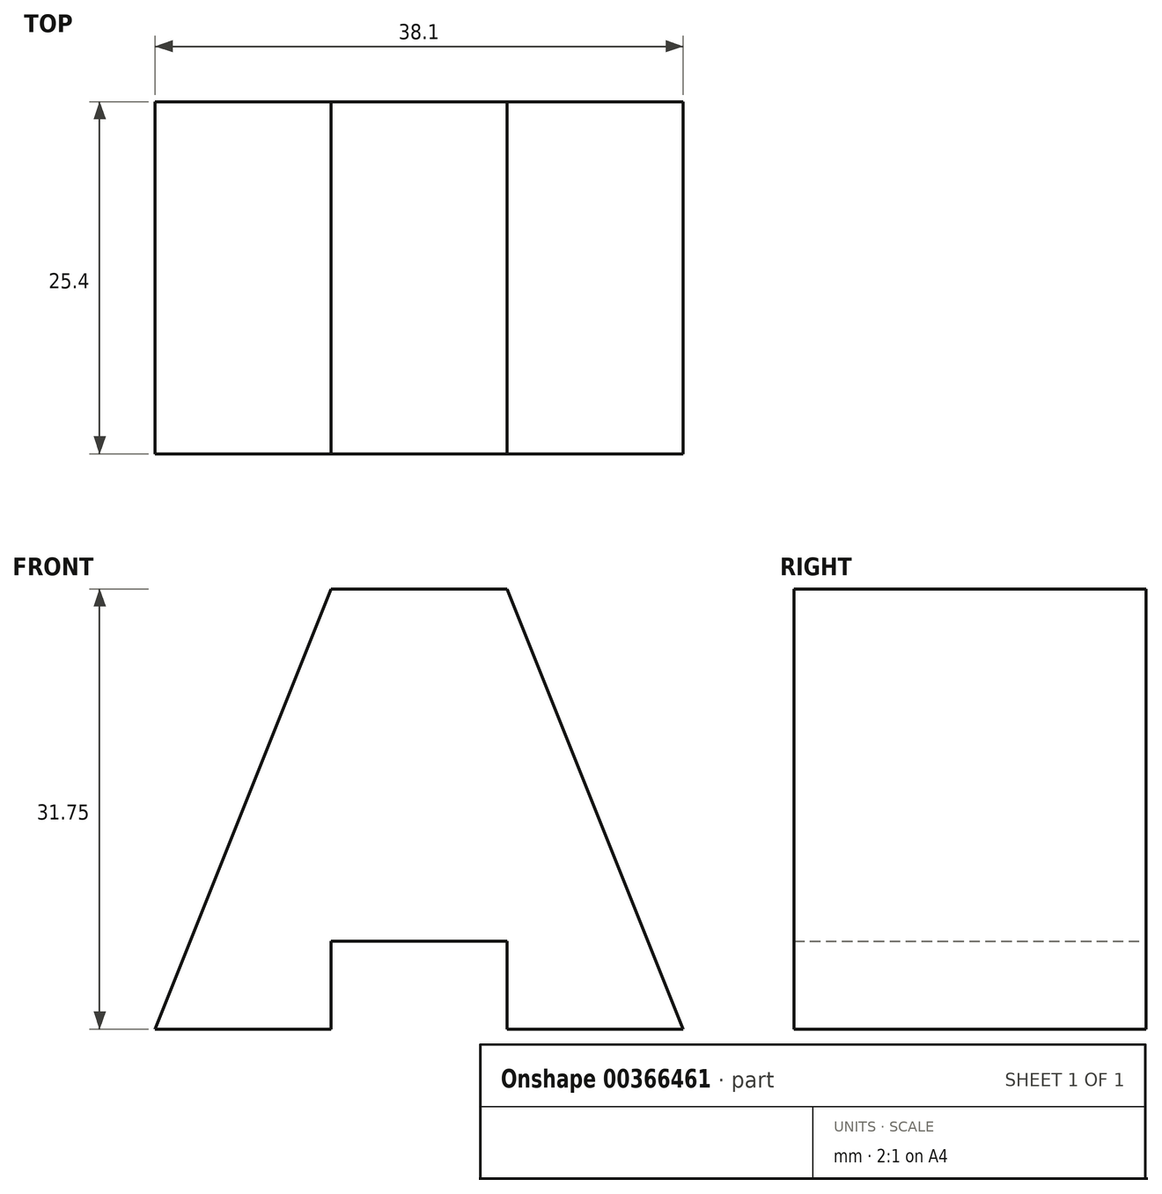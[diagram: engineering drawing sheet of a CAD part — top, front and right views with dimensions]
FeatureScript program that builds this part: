
annotation { "Feature Type Name" : "Feature", "Feature Type Description" : "" }
export const myFeature = defineFeature(function(context is Context, id is Id, definition is map)
    precondition{}
    {
        {
            var Q0;
            Q0=qCreatedBy(makeId("Front.planeOp"),FACE);
            var sketch = newSketch(context, id + "F0", { "sketchPlane" : qUnion([Q0])});
            skLineSegment(sketch, "E0", {"start": v(0, 0) * mm, "end": v(-12.7, 0) * mm});
            skLineSegment(sketch, "E1", {"start": v(-25.4, 0) * mm, "end": v(-38.1, 0) * mm});
            skLineSegment(sketch, "E2", {"start": v(-25.4, 0) * mm, "end": v(-25.4, 6.35) * mm});
            skLineSegment(sketch, "E3", {"start": v(-12.7, 0) * mm, "end": v(-12.7, 6.35) * mm});
            skLineSegment(sketch, "E4", {"start": v(-38.1, 0) * mm, "end": v(-25.4, 31.75) * mm});
            skLineSegment(sketch, "E5", {"start": v(0, 0) * mm, "end": v(-12.7, 31.75) * mm});
            skLineSegment(sketch, "E6", {"start": v(-25.4, 31.75) * mm, "end": v(-12.7, 31.75) * mm});
            skLineSegment(sketch, "E7", {"start": v(-25.4, 6.35) * mm, "end": v(-12.7, 6.35) * mm});
            skLineSegment(sketch, "E8", {"start": v(-12.7, 6.35) * mm, "end": v(-12.7, 0) * mm});
            skSolve(sketch);
        }
        {
            var Q0;
            Q0 = qSketchRegion(id + "F0", true);
            extrude(context, id + "F1", {"entities" : qUnion([Q0]), "depth" : 25.4 * mm});
        }
    });
